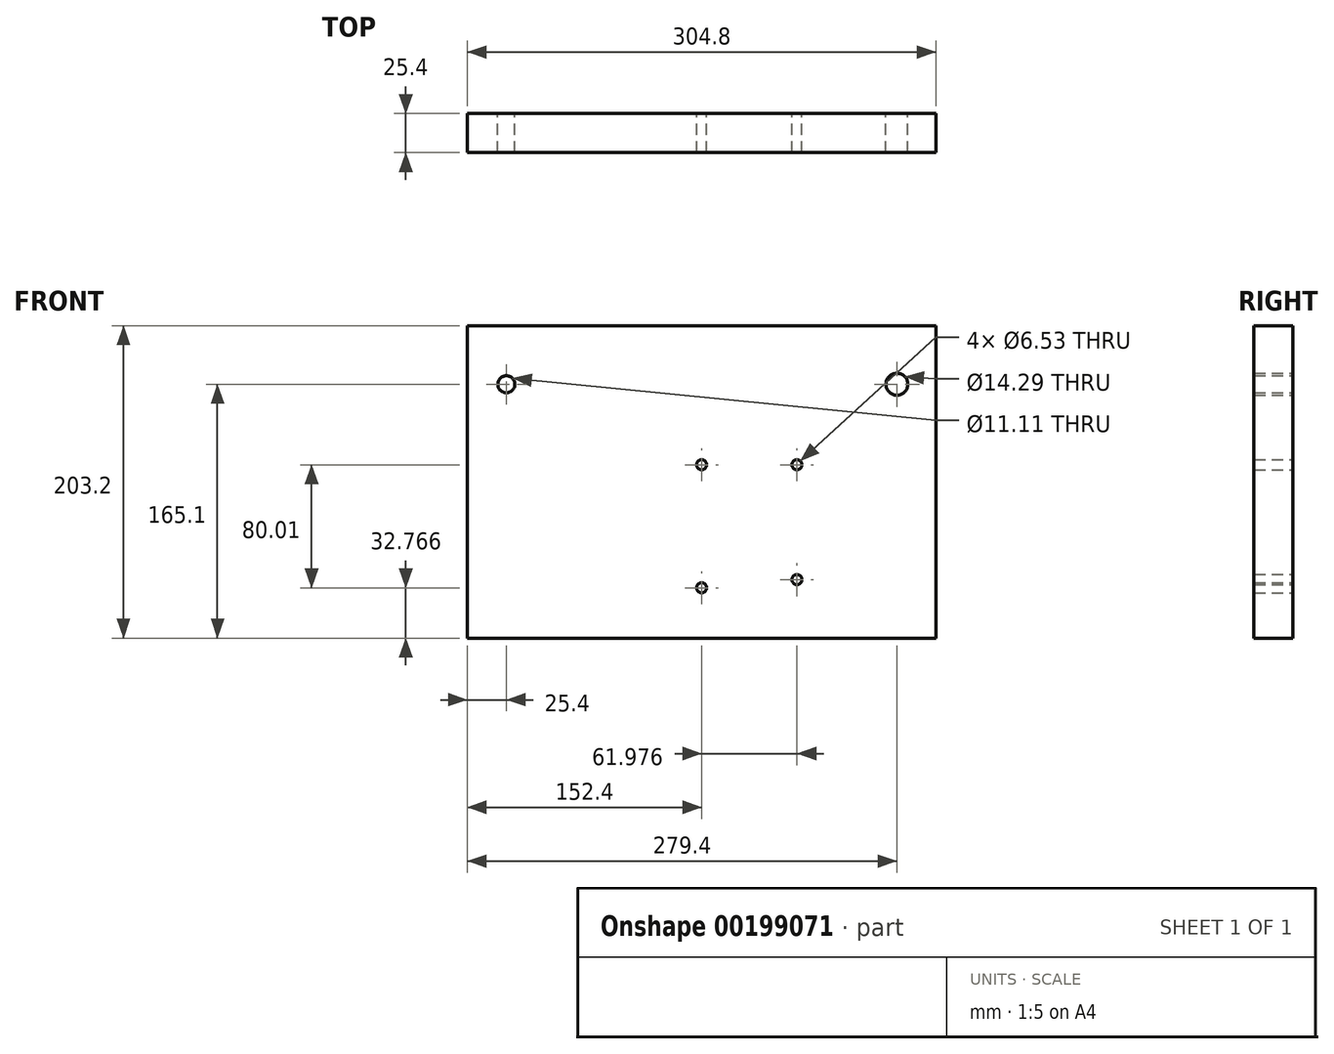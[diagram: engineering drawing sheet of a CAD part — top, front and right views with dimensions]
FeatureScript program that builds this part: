
annotation { "Feature Type Name" : "Feature", "Feature Type Description" : "" }
export const myFeature = defineFeature(function(context is Context, id is Id, definition is map)
    precondition{}
    {
        {
            var Q0;
            Q0=qCreatedBy(makeId("Front.planeOp"),FACE);
            var sketch = newSketch(context, id + "F0", { "sketchPlane" : qUnion([Q0])});
            skLineSegment(sketch, "E0.bottom", {"start": v(152.4, -101.6) * mm, "end": v(-152.4, -101.6) * mm});
            skLineSegment(sketch, "E0.top", {"start": v(152.4, 101.6) * mm, "end": v(-152.4, 101.6) * mm});
            skLineSegment(sketch, "E0.left", {"start": v(152.4, -101.6) * mm, "end": v(152.4, 101.6) * mm});
            skLineSegment(sketch, "E0.right", {"start": v(-152.4, -101.6) * mm, "end": v(-152.4, 101.6) * mm});
            skPoint(sketch, "E0.middle", {"position": v(0, 0) * mm});
            skLineSegment(sketch, "E1.bottom", {"start": v(0, -63.5) * mm, "end": v(61.98, -63.5) * mm});
            skLineSegment(sketch, "E1.top", {"start": v(0, 11.18) * mm, "end": v(61.98, 11.18) * mm});
            skLineSegment(sketch, "E1.left", {"start": v(0, -63.5) * mm, "end": v(0, 11.18) * mm});
            skLineSegment(sketch, "E1.right", {"start": v(61.98, -63.5) * mm, "end": v(61.98, 11.18) * mm});
            skCircle(sketch, "E2", {"center": v(127, 63.5) * mm, "radius": 7.14 * mm});
            skCircle(sketch, "E3", {"center": v(-127, 63.5) * mm, "radius": 5.56 * mm});
            skPoint(sketch, "E4", {"position": v(0, -68.83) * mm});
            skSolve(sketch);
        }
        {
            var Q0;
            Q0=makeQuery(id+"F0.imprint","IMPRINT",FACE,{"disambiguationData":[TD([[makeQuery(id+"F0.imprint","IMPRINT",EDGE,{"derivedFrom":sQuery(id+"F0.wireOp",EDGE,"E0.bottom")}),-1.0]])]});
            var Q1;
            Q1=makeQuery(id+"F0.imprint","IMPRINT",FACE,{"disambiguationData":[TD([[makeQuery(id+"F0.imprint","IMPRINT",EDGE,{"derivedFrom":sQuery(id+"F0.wireOp",EDGE,"E1.bottom")}),1.0]])]});
            extrude(context, id + "F1", {"entities" : qUnion([Q0, Q1]), "depth" : 25.4 * mm});
        }
        {
            var Q0;
            Q0=sQuery(id+"F0.wireOp",VERTEX,"E1.top.start");
            var Q1;
            Q1=sQuery(id+"F0.wireOp",VERTEX,"E1.top.end");
            var Q2;
            Q2=sQuery(id+"F0.wireOp",VERTEX,"E1.bottom.end");
            var Q3;
            Q3=sQuery(id+"F0.wireOp",VERTEX,"E4");
            var Q4;
            Q4=makeQuery(id+"F1.opExtrude","SWEPT_BODY",BODY,{"disambiguationData":[OSD([sQuery(id+"F0.wireOp",EDGE,"E0.bottom"),sQuery(id+"F0.wireOp",EDGE,"E0.top"),sQuery(id+"F0.wireOp",EDGE,"E0.left"),sQuery(id+"F0.wireOp",EDGE,"E0.right"),sQuery(id+"F0.wireOp",EDGE,"E2"),sQuery(id+"F0.wireOp",EDGE,"E3")])]});
            hole(context, id + "F2", {"style" : HoleStyle.SIMPLE, "endStyle" : HoleEndStyle.THROUGH, "oppositeDirection" : true, "standardTappedOrClearance" : lookupTablePath({ "standard" : "ANSI", "engagement" : "75%", "pitch" : "18 tpi", "size" : "5/16", "type" : "Tapped" }), "standardBlindInLast" : lookupTablePath({ "standard" : "ANSI", "engagement" : "75%", "pitch" : "18 tpi", "size" : "5/16", "type" : "Tapped" }), "holeDiameter" : 6.53 * mm, "locations" : qUnion([Q0, Q1, Q2, Q3]), "scope" : qUnion([Q4]), "isTappedThrough" : true, "majorDiameter" : 7.94 * mm, "showTappedDepth" : true});
        }
    });
